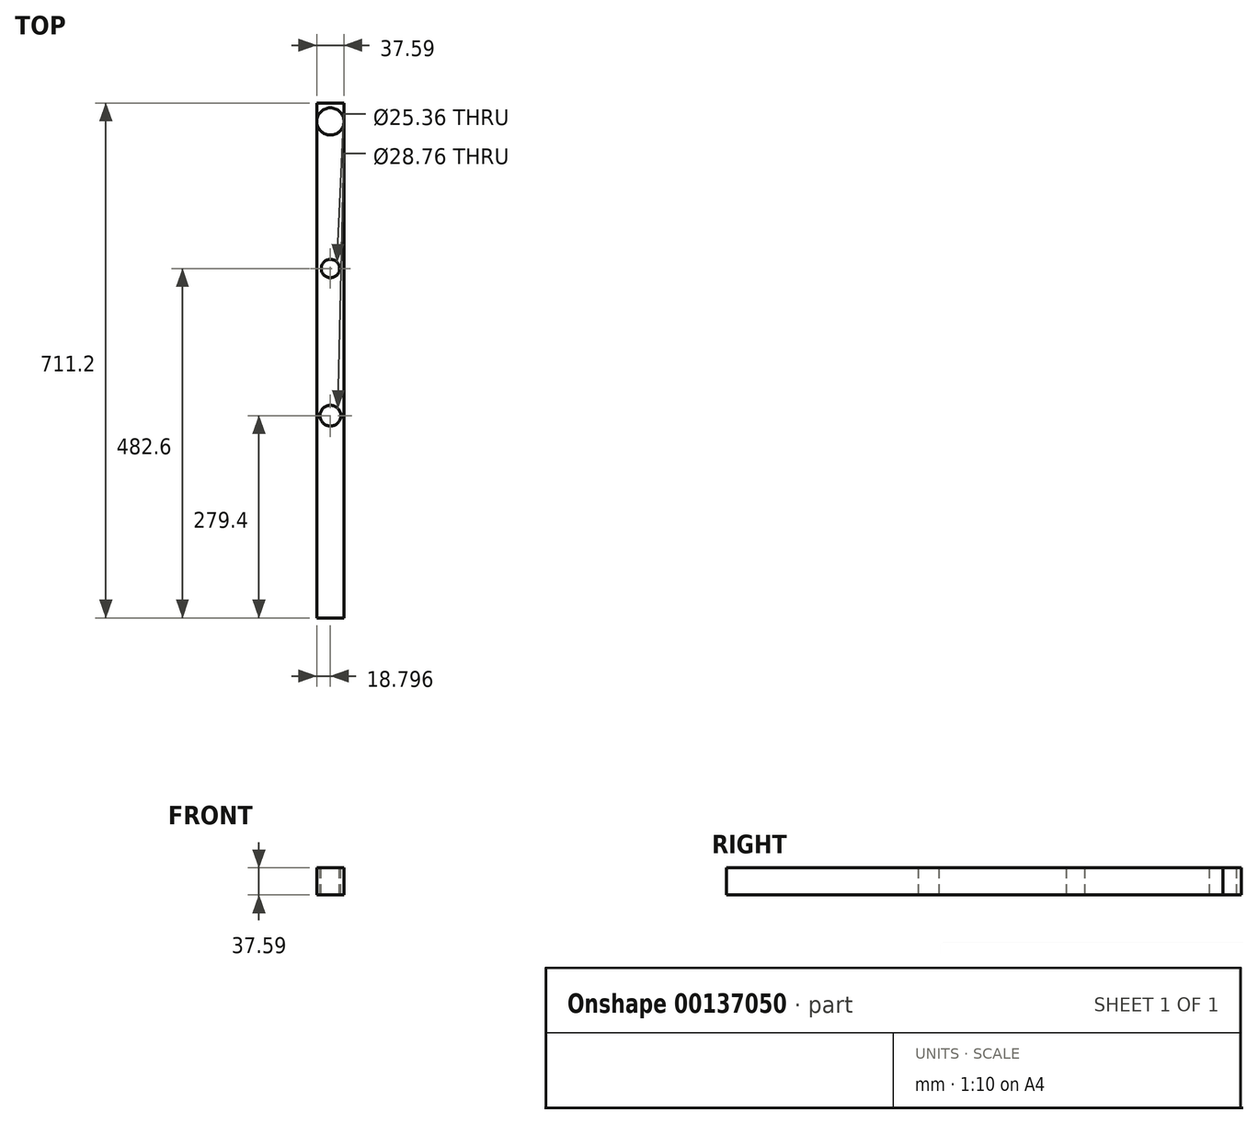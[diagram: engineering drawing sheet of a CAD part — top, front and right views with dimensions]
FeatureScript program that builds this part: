
annotation { "Feature Type Name" : "Feature", "Feature Type Description" : "" }
export const myFeature = defineFeature(function(context is Context, id is Id, definition is map)
    precondition{}
    {
        {
            var Q0;
            Q0=qCreatedBy(makeId("Front.planeOp"),FACE);
            var sketch = newSketch(context, id + "F0", { "sketchPlane" : qUnion([Q0])});
            skLineSegment(sketch, "E0.bottom", {"start": v(-8.65, -39.24) * mm, "end": v(-46.24, -39.24) * mm});
            skLineSegment(sketch, "E0.top", {"start": v(-8.65, -1.65) * mm, "end": v(-46.24, -1.65) * mm});
            skLineSegment(sketch, "E0.left", {"start": v(-8.65, -39.24) * mm, "end": v(-8.65, -1.65) * mm});
            skLineSegment(sketch, "E0.right", {"start": v(-46.24, -39.24) * mm, "end": v(-46.24, -1.65) * mm});
            skPoint(sketch, "E0.middle", {"position": v(-27.44, -20.45) * mm});
            skSolve(sketch);
        }
        {
            var Q0;
            Q0 = qSketchRegion(id + "F0", true);
            extrude(context, id + "F1", {"entities" : qUnion([Q0]), "depth" : 711.2 * mm});
        }
        {
            var Q0;
            Q0=makeQuery(id+"F1.opExtrude","SWEPT_FACE",FACE,{"disambiguationData":[OSD([sQuery(id+"F0.wireOp",EDGE,"E0.top")])]});
            var sketch = newSketch(context, id + "F2", { "sketchPlane" : qUnion([Q0])});
            skPoint(sketch, "E1.start.orphan", {"position": v(-27.44, -711.2) * mm});
            skLineSegment(sketch, "E2", {"start": v(-27.44, -446.18) * mm, "end": v(-27.44, -431.8) * mm});
            skCircle(sketch, "E3", {"center": v(-27.44, -431.8) * mm, "radius": 14.38 * mm});
            skLineSegment(sketch, "E4", {"start": v(-27.44, -431.8) * mm, "end": v(-27.44, -417.42) * mm});
            skCircle(sketch, "E5", {"center": v(-27.44, -228.6) * mm, "radius": 12.68 * mm});
            skLineSegment(sketch, "E6.trimOffspring", {"start": v(-27.44, -241.28) * mm, "end": v(-27.44, -228.6) * mm});
            skLineSegment(sketch, "E7", {"start": v(-27.44, -228.6) * mm, "end": v(-27.44, -215.92) * mm});
            skCircle(sketch, "E8", {"center": v(-27.44, -25.4) * mm, "radius": 18.8 * mm});
            skLineSegment(sketch, "E9.trimOffspring", {"start": v(-27.44, -44.2) * mm, "end": v(-27.44, -25.4) * mm});
            skSolve(sketch);
        }
        {
            var Q0;
            Q0 = qSketchRegion(id + "F2", true);
            extrude(context, id + "F3", {"entities" : qUnion([Q0]), "operationType" : NewBodyOperationType.REMOVE, "endBound" : BoundingType.THROUGH_ALL, "oppositeDirection" : true, "depth" : 25.4 * mm});
        }
    });
